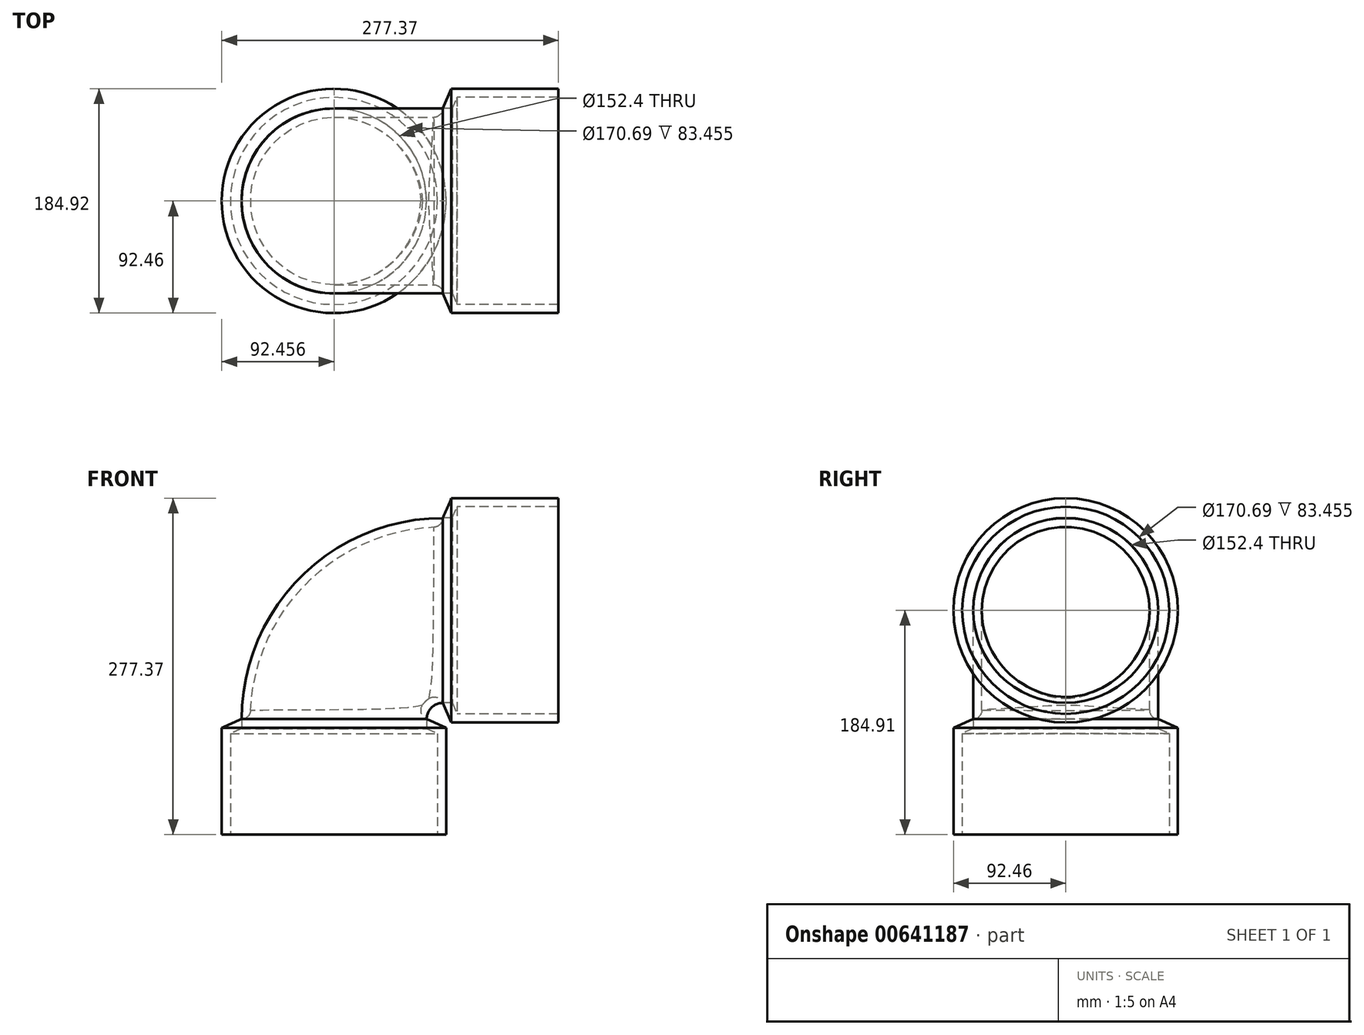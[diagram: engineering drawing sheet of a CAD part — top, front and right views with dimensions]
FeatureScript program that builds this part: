
annotation { "Feature Type Name" : "Feature", "Feature Type Description" : "" }
export const myFeature = defineFeature(function(context is Context, id is Id, definition is map)
    precondition{}
    {
        {
            var Q0;
            Q0=qCreatedBy(makeId("Front.planeOp"),FACE);
            var sketch = newSketch(context, id + "F0", { "sketchPlane" : qUnion([Q0])});
            skLineSegment(sketch, "E0", {"start": v(0, 0) * mm, "end": v(0, 76.2) * mm});
            skLineSegment(sketch, "E1", {"start": v(0, 0) * mm, "end": v(7.11, 0) * mm});
            skLineSegment(sketch, "E2", {"start": v(7.11, 0) * mm, "end": v(95.22, 0) * mm});
            skLineSegment(sketch, "E3.0", {"start": v(7.11, 92.46) * mm, "end": v(95.22, 92.46) * mm});
            skLineSegment(sketch, "E4", {"start": v(7.11, 92.46) * mm, "end": v(0, 76.2) * mm});
            skLineSegment(sketch, "E5.0", {"start": v(11.76, 85.34) * mm, "end": v(7.76, 76.2) * mm});
            skLineSegment(sketch, "E5.1", {"start": v(11.76, 85.34) * mm, "end": v(95.22, 85.34) * mm});
            skLineSegment(sketch, "E6", {"start": v(95.22, 92.46) * mm, "end": v(95.22, 85.34) * mm});
            skLineSegment(sketch, "E7", {"start": v(0, 76.2) * mm, "end": v(7.76, 76.2) * mm});
            skSolve(sketch);
        }
        {
            var Q0;
            Q0=qCreatedBy(makeId("Right.planeOp"),FACE);
            var sketch = newSketch(context, id + "F1", { "sketchPlane" : qUnion([Q0])});
            skCircle(sketch, "E8", {"center": v(0, -0.17) * mm, "radius": 76.2 * mm});
            skCircle(sketch, "E9.0", {"center": v(0, -0.17) * mm, "radius": 69.09 * mm});
            skSolve(sketch);
        }
        {
            var Q0;
            Q0=qCreatedBy(makeId("Front.planeOp"),FACE);
            var sketch = newSketch(context, id + "F2", { "sketchPlane" : qUnion([Q0])});
            skLineSegment(sketch, "E10", {"start": v(0, -118.12) * mm, "end": v(0, -197.38) * mm});
            skLineSegment(sketch, "E11", {"start": v(0, -197.38) * mm, "end": v(-166.69, -197.38) * mm});
            skLineSegment(sketch, "E12.0", {"start": v(-89.7, -184.91) * mm, "end": v(-89.7, -89.7) * mm});
            skLineSegment(sketch, "E13.0", {"start": v(-182.15, -184.91) * mm, "end": v(-182.15, -96.8) * mm});
            skLineSegment(sketch, "E14", {"start": v(-89.7, -89.7) * mm, "end": v(-165.9, -89.7) * mm});
            skLineSegment(sketch, "E15", {"start": v(-165.9, -89.7) * mm, "end": v(-182.15, -96.8) * mm});
            skLineSegment(sketch, "E16.0", {"start": v(-175.04, -184.91) * mm, "end": v(-175.04, -101.46) * mm});
            skLineSegment(sketch, "E16.1", {"start": v(-165.9, -97.46) * mm, "end": v(-175.04, -101.46) * mm});
            skLineSegment(sketch, "E17", {"start": v(-165.9, -89.7) * mm, "end": v(-165.9, -97.46) * mm});
            skLineSegment(sketch, "E18", {"start": v(-182.15, -184.91) * mm, "end": v(-175.04, -184.91) * mm});
            skLineSegment(sketch, "E19", {"start": v(0, 0) * mm, "end": v(-89.7, 0) * mm});
            skLineSegment(sketch, "E20", {"start": v(-89.7, 0) * mm, "end": v(-89.7, -89.7) * mm});
            skSolve(sketch);
        }
        {
            var Q0;
            Q0=qCreatedBy(makeId("Front.planeOp"),FACE);
            var sketch = newSketch(context, id + "F3", { "sketchPlane" : qUnion([Q0])});
            skLineSegment(sketch, "E21", {"start": v(0, -155.26) * mm, "end": v(0, -148.15) * mm});
            skLineSegment(sketch, "E22", {"start": v(0, -148.15) * mm, "end": v(-89.7, -148.15) * mm});
            skLineSegment(sketch, "E23", {"start": v(0, 0) * mm, "end": v(0, 0) * mm});
            skLineSegment(sketch, "E24", {"start": v(-89.7, -89.7) * mm, "end": v(-89.7, -89.7) * mm});
            skPoint(sketch, "E25.visualSharp", {"position": v(-89.7, 0) * mm});
            skArc(sketch, "E25.filletArc", {"start": v(0, 0) * mm, "mid": v(-63.42, -26.27) * mm, "end": v(-89.7, -89.7) * mm});
            skSolve(sketch);
        }
        {
            var Q0;
            Q0=makeQuery(id+"F0.imprint","IMPRINT",FACE,{"disambiguationData":[TD([[makeQuery(id+"F0.imprint","IMPRINT",EDGE,{"derivedFrom":sQuery(id+"F0.wireOp",EDGE,"E3.0")}),-1.0]])]});
            var Q1;
            Q1=sQuery(id+"F0.wireOp",EDGE,"E2");
            revolve(context, id + "F4", {"entities" : qUnion([Q0]), "axis" : qUnion([Q1]), "revolveType" : RevolveType.FULL});
        }
        {
            var Q0;
            Q0=makeQuery(id+"F1.imprint","IMPRINT",FACE,{"disambiguationData":[TD([[makeQuery(id+"F1.imprint","IMPRINT",EDGE,{"derivedFrom":sQuery(id+"F1.wireOp",EDGE,"E8")}),1.0]])]});
            var Q1;
            Q1=sQuery(id+"F3.wireOp",EDGE,"E25.filletArc");
            sweep(context, id + "F5", {"operationType" : NewBodyOperationType.ADD, "profiles" : qUnion([Q0]), "path" : qUnion([Q1])});
        }
        {
            var Q0;
            Q0=makeQuery(id+"F2.imprint","IMPRINT",FACE,{"disambiguationData":[TD([[makeQuery(id+"F2.imprint","IMPRINT",EDGE,{"derivedFrom":sQuery(id+"F2.wireOp",EDGE,"E13.0")}),-1.0]])]});
            var Q1;
            Q1=sQuery(id+"F2.wireOp",EDGE,"E12.0");
            revolve(context, id + "F6", {"operationType" : NewBodyOperationType.ADD, "entities" : qUnion([Q0]), "axis" : qUnion([Q1]), "revolveType" : RevolveType.FULL});
        }
        {
            var Q0;
            Q0=makeQuery(id+"F5.opSweep","CAP_EDGE",EDGE,{"disambiguationData":[OSD([sQuery(id+"F1.wireOp",EDGE,"E9.0"),sQuery(id+"F3.wireOp",VERTEX,"E25.filletArc.start")])],"isStart":true});
            var Q1;
            Q1=makeQuery(id+"F5.opSweep","CAP_EDGE",EDGE,{"disambiguationData":[OSD([sQuery(id+"F1.wireOp",EDGE,"E9.0"),sQuery(id+"F3.wireOp",VERTEX,"E25.filletArc.end")])],"isStart":false});
            fillet(context, id + "F7", {"entities" : qUnion([Q0, Q1]), "radius" : 7.62 * mm, "tangentPropagation" : true, "allowEdgeOverflow" : false});
        }
    });
